# Revit family: Холодильные шкафы со стеклянными дверьми POLAIR Bravo
name_source: partatom
category: Оборудование
units: mm (PartAtom-declared; Revit-internal decimal feet)

## family parameters
Всегда вертикально = Да
Классификация = Нет
На основе рабочей плоскости = Нет
Общий = Нет
При загрузке вырезать с полостями = Нет
Размер круглого соединителя = Использовать диаметр
Тип детали = Нормальный
Точка расчета площади = Нет

## types (6) — shared parameters
Диап. рабочих температур = +1....+10
Допустимая нагрузка на полку, кг = 40
Тип охлаждения = динамический
Хладагент = R134a
Холодильный шкаф = <По категории>
Ширина = 606 мм
zero-valued in all types: Отметка по умолчанию

## per-type parameters (varying)
| type | 2 полки | 4 полки | Верхний агрегат | Вес брутто, кг | Вес нетто, кг | Высота | Высота агрегата | Габаритные размеры, мм | Глубина | Замок | Кол-во полок | Объем, л. | Подсветка | Потребляемая мощность, Вт, не более | Размер полки, мм | Размеры в упаковке, мм | Расход электроэнергии за сутки, кВт/ч | Ролики | Система электропитания В/Гц | Терморегулятор | Условия окр. среды (темп./вл-сть,%) | Цена, руб. |
| DM104c-Bravo | Нет | Да | Да | 107 | 87 | 1935 мм | 205 мм | 606х600х1935 | 600 мм | Нет | 4 | 390 | LED, вертикальная | 240 |  | 720х660х2100 | 2,4 | + | 220-240/50 | термостат | 12-32/60 | 38 334 |
| DM102-Bravo | Да | Нет | Нет | 65 | 58 | 890 мм | 56 мм | 606х625х890 | 625 мм | Нет | 2 | 150 | LED |  | 505*455 | 720х660х1100 |  |  | 230/50 | эл.  блок | до +32/до 60 | 32 900 |
| DM104-Bravo | Нет | Да | Нет | 102 | 82 | 1730 мм | 1 мм | 606х600х1730 | 600 мм | Нет | 4 | 390 | LED | 240 |  | 720х660х1900 | 2,2 | + | 220-240/50 | термостат | 12-32/60 | 37 907 |
| DM102-Bravo с замком | Да | Нет | Нет | 65 | 58 | 890 мм | 56 мм | 606х625х890 | 625 мм | Да | 2 | 150 | LED | 0,55 раб./0,40 отт. | 505*455 | 720х660х1100 | 12,5 |  | 230/50 | эл.  блок | до +32/до 60 | 34 324 |
| DM102-Bravo черный | Да | Нет | Нет | 65 | 58 | 890 мм | 56 мм | 606х625х890 | 625 мм | Нет | 2 | 150 | LED |  | 505*455 | 720х660х1100 |  |  | 230/50 | эл.  блок | до +32/до 60 | 34 734 |
| DM102-Bravo черный с замком | Да | Нет | Нет | 65 | 58 | 890 мм | 56 мм | 606х625х890 | 625 мм | Да | 2 | 150 | LED |  | 505*455 | 720х660х1100 |  |  | 230/50 | эл.  блок | до +32/до 60 | 36 160 |
